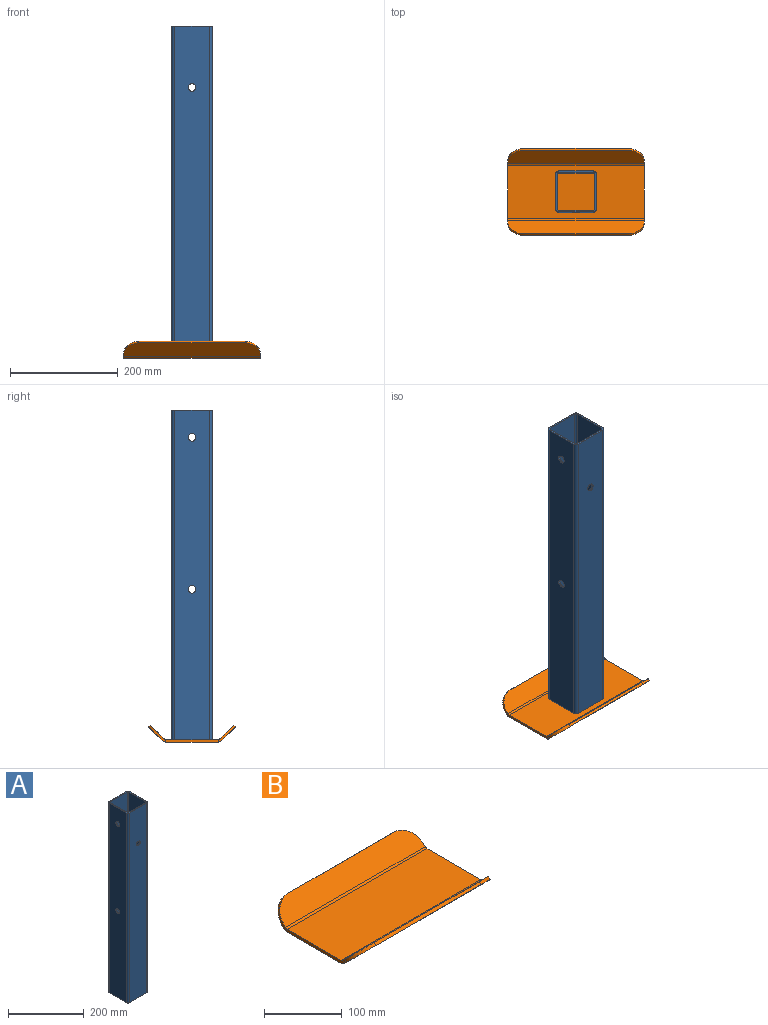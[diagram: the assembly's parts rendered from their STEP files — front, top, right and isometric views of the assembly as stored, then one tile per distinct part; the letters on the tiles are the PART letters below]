
ASSEMBLY  parts=2 mates=1
PART A: 24 faces, bbox 76.2x76.2x612.8 mm
  f0: cylinder r=3.3mm len=612.78mm, axis (0,0,-1), area 3178.3mm2, adj f1,f15,f16,f17
  f1: plane 612.78x63.5mm, normal (-1,0,0), area 38590.6mm2, adj f0,f2,f16,f17,f22,f23
  f2: cylinder r=3.3mm len=612.78mm, axis (0,0,-1), area 3178.3mm2, adj f1,f3,f16,f17
  f3: plane 612.78x63.5mm, normal (0,1,0), area 38750.9mm2, adj f2,f4,f16,f17,f19
  f4: cylinder r=3.3mm len=612.78mm, axis (0,0,-1), area 3178.3mm2, adj f3,f5,f16,f17
  f5: plane 612.78x63.5mm, normal (1,0,0), area 38590.6mm2, adj f4,f6,f16,f17,f20,f21
  f6: cylinder r=3.3mm len=612.78mm, axis (0,0,-1), area 3178.3mm2, adj f5,f15,f16,f17
  f7: plane 612.78x63.5mm, normal (1,0,0), area 38590.6mm2, adj f8,f14,f16,f17,f22,f23
  f8: cylinder r=6.35mm len=612.78mm, axis (0,0,-1), area 6112.2mm2, adj f7,f9,f16,f17
  f9: plane 612.78x63.5mm, normal (0,1,0), area 38750.9mm2, adj f8,f10,f16,f17,f18
  f10: cylinder r=6.35mm len=612.78mm, axis (0,0,-1), area 6112.2mm2, adj f9,f11,f16,f17
  f11: plane 612.78x63.5mm, normal (-1,0,0), area 38590.6mm2, adj f10,f12,f16,f17,f20,f21
  f12: cylinder r=6.35mm len=612.78mm, axis (0,0,-1), area 6112.2mm2, adj f11,f13,f16,f17
  f13: plane 612.78x63.5mm, normal (0,-1,0), area 38750.9mm2, adj f12,f14,f16,f17,f19
  f14: cylinder r=6.35mm len=612.78mm, axis (0,0,-1), area 6112.2mm2, adj f7,f13,f16,f17
  f15: plane 612.78x63.5mm, normal (0,-1,0), area 38750.9mm2, adj f0,f6,f16,f17,f18
  f16: plane 76.2x76.2mm, normal (0,0,1), area 866.6mm2, adj f0,f1,f2,f3,f4,f5,f6,f7
  f17: plane 76.2x76.2mm, normal (0,0,-1), area 866.6mm2, adj f0,f1,f2,f3,f4,f5,f6,f7
  f18: cylinder r=7.14mm len=14.29mm, axis (0,-1,0), area 136.8mm2, adj f9,f15
  f19: cylinder r=7.14mm len=14.29mm, axis (0,-1,0), area 136.8mm2, adj f3,f13
  f20: cylinder r=7.14mm len=14.29mm, axis (1,0,0), area 136.8mm2, adj f5,f11
  f21: cylinder r=7.14mm len=14.29mm, axis (1,0,0), area 136.8mm2, adj f5,f11
  f22: cylinder r=7.14mm len=14.29mm, axis (1,0,0), area 136.8mm2, adj f1,f7
  f23: cylinder r=7.14mm len=14.29mm, axis (1,0,0), area 136.8mm2, adj f1,f7
PART B: 26 faces, bbox 254x162x31.6 mm
  f0: plane 97.65x4.55mm, normal (-1,0,0), area 444mm2, adj f2,f3,f12,f23
  f1: plane 97.65x4.55mm, normal (1,0,0), area 444mm2, adj f2,f3,f11,f22
  f2: plane 254x97.65mm, normal (0,0,-1), area 24804.3mm2, adj f0,f1,f13,f24
  f3: plane 254x97.65mm, normal (0,0,1), area 24804.3mm2, adj f0,f1,f14,f25
  f4: plane 6.38x6.38mm, normal (-1,0,0), area 20.3mm2, adj f7,f8,f9,f12
  f5: plane 190.5x3.22mm, normal (0,0.71,0.71), area 866.1mm2, adj f7,f8,f9,f10
  f6: plane 6.38x6.38mm, normal (1,0,0), area 20.3mm2, adj f7,f8,f10,f11
  f7: plane 254x25.61mm, normal (0,0.71,-0.71), area 8767.6mm2, adj f4,f5,f6,f9,f10,f13
  f8: plane 254x25.61mm, normal (0,-0.71,0.71), area 8767.6mm2, adj f4,f5,f6,f9,f10,f14
  f9: cylinder r=31.75mm len=31.75mm, axis (0,-0.71,0.71), area 226.8mm2, adj f4,f5,f7,f8
  f10: cylinder r=31.75mm len=31.75mm, axis (0,0.71,-0.71), area 226.8mm2, adj f5,f6,f7,f8
  f11: plane 6.58x5.94mm, normal (1,0,0), area 25.1mm2, adj f1,f6,f13,f14
  f12: plane 6.58x5.94mm, normal (-1,0,0), area 25.1mm2, adj f0,f4,f13,f14
  f13: cylinder r=9.31mm len=254mm, axis (1,0,0), area 1857.1mm2, adj f2,f7,f11,f12
  f14: cylinder r=4.76mm len=254mm, axis (1,0,0), area 950.1mm2, adj f3,f8,f11,f12
  f15: plane 6.38x6.38mm, normal (-1,0,0), area 20.3mm2, adj f18,f19,f21,f23
  f16: plane 6.38x6.38mm, normal (1,0,0), area 20.3mm2, adj f18,f19,f20,f22
  f17: plane 190.5x3.22mm, normal (0,-0.71,0.71), area 866.1mm2, adj f18,f19,f20,f21
  f18: plane 254x25.61mm, normal (0,-0.71,-0.71), area 8767.6mm2, adj f15,f16,f17,f20,f21,f24
  f19: plane 254x25.61mm, normal (0,0.71,0.71), area 8767.6mm2, adj f15,f16,f17,f20,f21,f25
  f20: cylinder r=31.75mm len=31.75mm, axis (0,-0.71,-0.71), area 226.8mm2, adj f16,f17,f18,f19
  f21: cylinder r=31.75mm len=31.75mm, axis (0,0.71,0.71), area 226.8mm2, adj f15,f17,f18,f19
  f22: plane 6.58x5.94mm, normal (1,0,0), area 25.1mm2, adj f1,f16,f24,f25
  f23: plane 6.58x5.94mm, normal (-1,0,0), area 25.1mm2, adj f0,f15,f24,f25
  f24: cylinder r=9.31mm len=254mm, axis (1,0,0), area 1857.1mm2, adj f2,f18,f22,f23
  f25: cylinder r=4.76mm len=254mm, axis (1,0,0), area 950.1mm2, adj f3,f19,f22,f23
PLACE A t=(-47.91,0.57,414.42)mm
PLACE B t=(79.09,0.57,108.03)mm
MATE planar B.f3 <-> A.f17  axis (0,0,1) through (-47.91,0.57,108.03)mm
